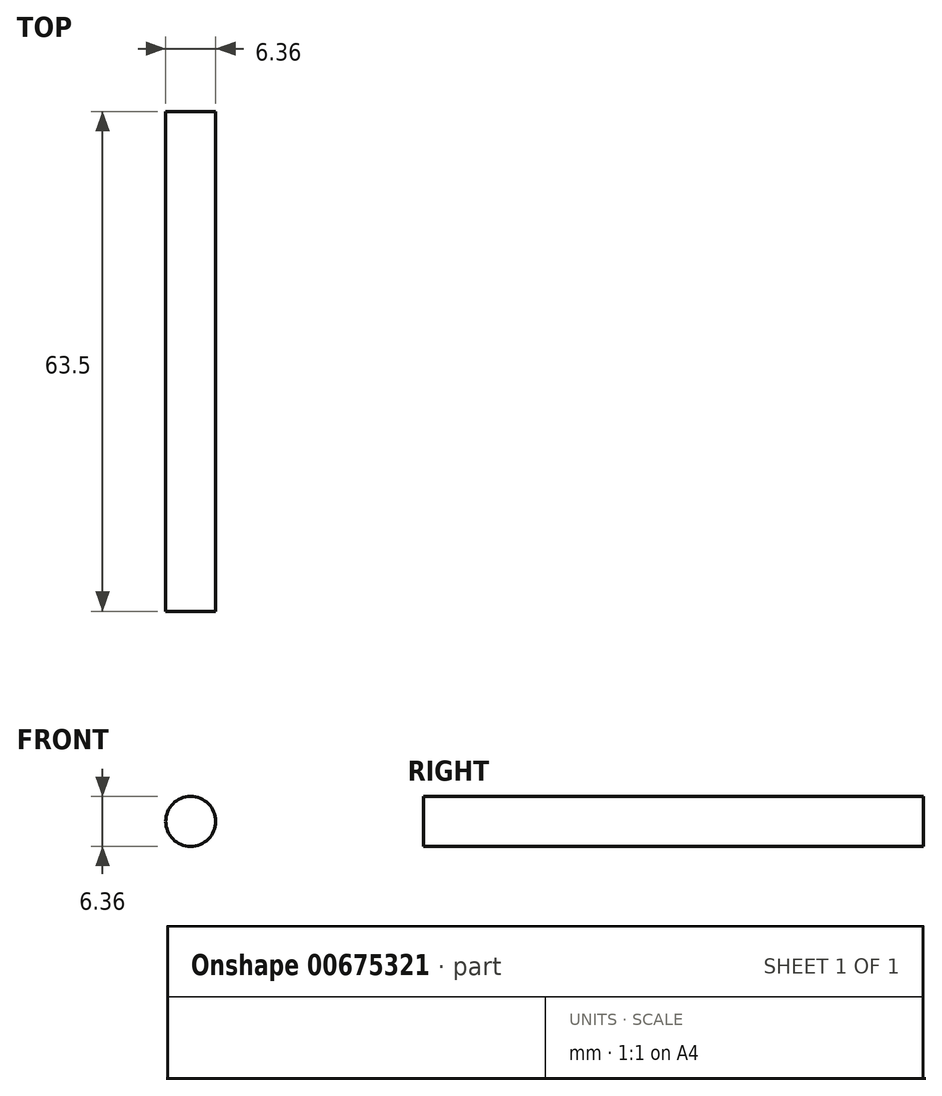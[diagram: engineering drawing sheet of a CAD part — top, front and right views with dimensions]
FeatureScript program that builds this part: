
annotation { "Feature Type Name" : "Feature", "Feature Type Description" : "" }
export const myFeature = defineFeature(function(context is Context, id is Id, definition is map)
    precondition{}
    {
        {
            var Q0;
            Q0=qCreatedBy(makeId("Front.planeOp"),FACE);
            var sketch = newSketch(context, id + "F0", { "sketchPlane" : qUnion([Q0])});
            skCircle(sketch, "E0", {"center": v(0, 0) * mm, "radius": 3.18 * mm});
            skSolve(sketch);
        }
        {
            var Q0;
            Q0 = qSketchRegion(id + "F0", true);
            extrude(context, id + "F1", {"entities" : qUnion([Q0]), "oppositeDirection" : true, "depth" : 63.5 * mm, "offsetDistance" : 25.4 * mm});
        }
    });
